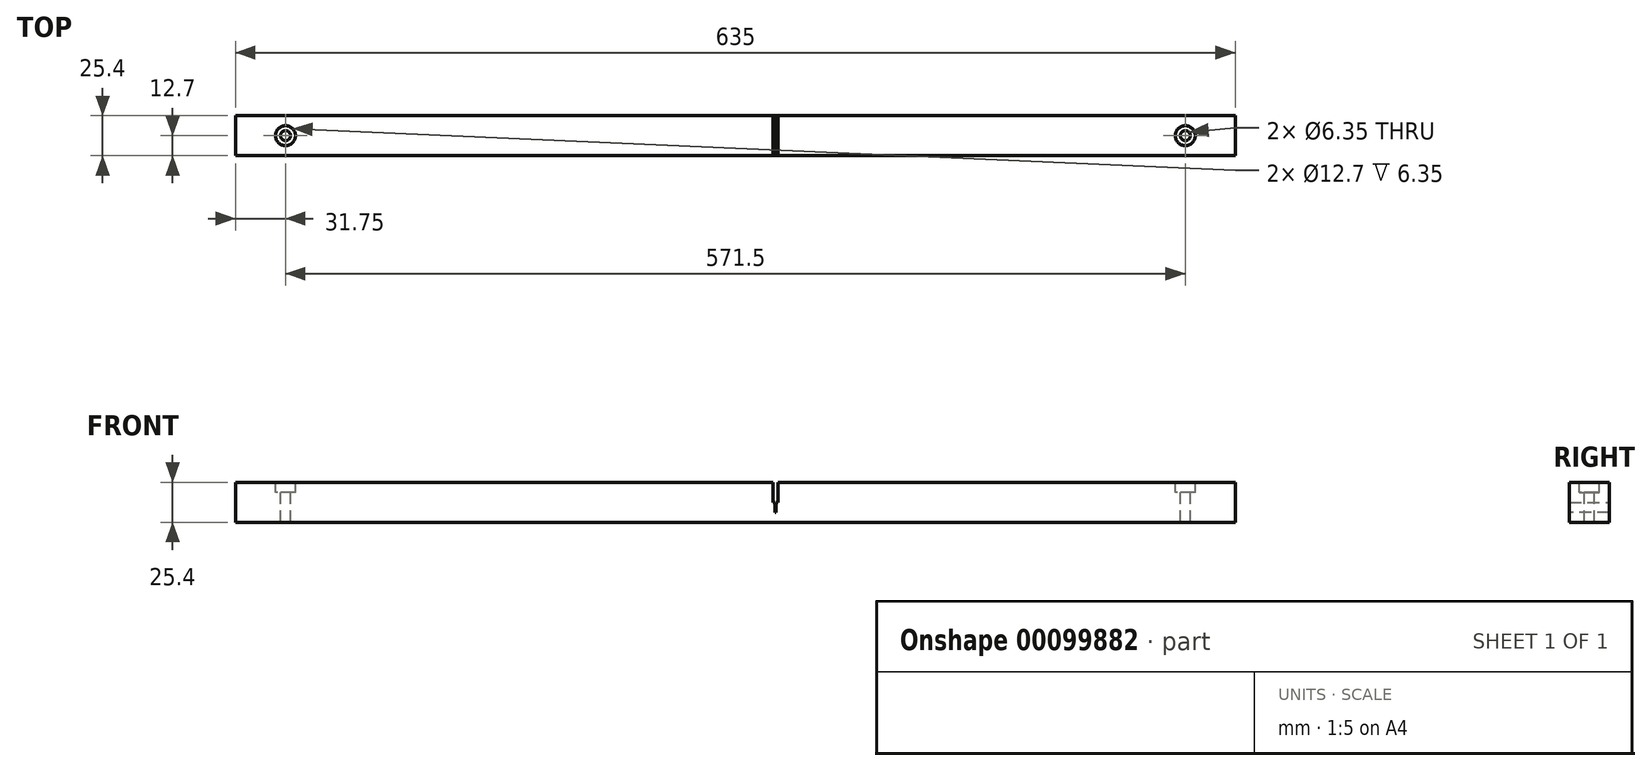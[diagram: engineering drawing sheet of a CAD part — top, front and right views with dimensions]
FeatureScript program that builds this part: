
annotation { "Feature Type Name" : "Feature", "Feature Type Description" : "" }
export const myFeature = defineFeature(function(context is Context, id is Id, definition is map)
    precondition{}
    {
        {
            var Q0;
            Q0=qCreatedBy(makeId("Top.planeOp"),FACE);
            var sketch = newSketch(context, id + "F0", { "sketchPlane" : qUnion([Q0])});
            skLineSegment(sketch, "E0.bottom", {"start": v(317.5, -12.7) * mm, "end": v(-317.5, -12.7) * mm});
            skLineSegment(sketch, "E0.top", {"start": v(317.5, 12.7) * mm, "end": v(-317.5, 12.7) * mm});
            skLineSegment(sketch, "E0.left", {"start": v(317.5, -12.7) * mm, "end": v(317.5, 12.7) * mm});
            skLineSegment(sketch, "E0.right", {"start": v(-317.5, -12.7) * mm, "end": v(-317.5, 12.7) * mm});
            skPoint(sketch, "E0.middle", {"position": v(0, 0) * mm});
            skSolve(sketch);
        }
        {
            var Q0;
            Q0=makeQuery(id+"F0.imprint","IMPRINT",FACE,{"disambiguationData":[TD([[makeQuery(id+"F0.imprint","IMPRINT",EDGE,{"derivedFrom":sQuery(id+"F0.wireOp",EDGE,"E0.bottom")}),-1.0]])]});
            extrude(context, id + "F1", {"entities" : qUnion([Q0]), "depth" : 25.4 * mm});
        }
        {
            var Q0;
            Q0=makeQuery(id+"F1.opExtrude","CAP_FACE",FACE,{"disambiguationData":[OSD([sQuery(id+"F0.wireOp",EDGE,"E0.bottom"),sQuery(id+"F0.wireOp",EDGE,"E0.top"),sQuery(id+"F0.wireOp",EDGE,"E0.left"),sQuery(id+"F0.wireOp",EDGE,"E0.right")])],"isStart":false});
            var sketch = newSketch(context, id + "F2", { "sketchPlane" : qUnion([Q0])});
            skPoint(sketch, "E1", {"position": v(-285.75, 0) * mm});
            skPoint(sketch, "E2.MirrorP", {"position": v(285.75, 0) * mm});
            skSolve(sketch);
        }
        {
            var Q0;
            Q0=sQuery(id+"F2.wireOp",VERTEX,"E1");
            var Q1;
            Q1=sQuery(id+"F2.wireOp",VERTEX,"E2.MirrorP");
            var Q2;
            Q2=makeQuery(id+"F1.opExtrude","SWEPT_BODY",BODY,{"disambiguationData":[OSD([sQuery(id+"F0.wireOp",EDGE,"E0.bottom"),sQuery(id+"F0.wireOp",EDGE,"E0.top"),sQuery(id+"F0.wireOp",EDGE,"E0.left"),sQuery(id+"F0.wireOp",EDGE,"E0.right")])]});
            hole(context, id + "F3", {"style" : HoleStyle.C_BORE, "endStyle" : HoleEndStyle.THROUGH, "holeDiameter" : 6.35 * mm, "cBoreDiameter" : 12.7 * mm, "cBoreDepth" : 6.35 * mm, "locations" : qUnion([Q0, Q1]), "scope" : qUnion([Q2]), "isTappedThrough" : true});
        }
        {
            var Q0;
            Q0=makeQuery(id+"F1.opExtrude","CAP_FACE",FACE,{"disambiguationData":[OSD([sQuery(id+"F0.wireOp",EDGE,"E0.bottom"),sQuery(id+"F0.wireOp",EDGE,"E0.top"),sQuery(id+"F0.wireOp",EDGE,"E0.left"),sQuery(id+"F0.wireOp",EDGE,"E0.right")])],"isStart":false});
            var sketch = newSketch(context, id + "F4", { "sketchPlane" : qUnion([Q0])});
            skLineSegment(sketch, "E3.bottom", {"start": v(25.1, 12.7) * mm, "end": v(25.7, 12.7) * mm});
            skLineSegment(sketch, "E3.top", {"start": v(25.1, -12.7) * mm, "end": v(25.7, -12.7) * mm});
            skLineSegment(sketch, "E3.left", {"start": v(25.1, 12.7) * mm, "end": v(25.1, -12.7) * mm});
            skLineSegment(sketch, "E3.right", {"start": v(25.7, 12.7) * mm, "end": v(25.7, -12.7) * mm});
            skPoint(sketch, "E3.middle", {"position": v(25.4, 0) * mm});
            skSolve(sketch);
        }
        {
            var Q0;
            Q0 = qSketchRegion(id + "F4", true);
            extrude(context, id + "F5", {"entities" : qUnion([Q0]), "operationType" : NewBodyOperationType.REMOVE, "oppositeDirection" : true, "depth" : 19.05 * mm});
        }
        {
            var Q0;
            {var subQ0=sQuery(id+"F0.wireOp",EDGE,"E0.right");var subQ1=sQuery(id+"F0.wireOp",EDGE,"E0.top");var subQ2=sQuery(id+"F0.wireOp",EDGE,"E0.bottom");Q0=makeQuery(id+"F5.boolean.opBoolean","SPLIT",FACE,{"disambiguationData":[TD([makeQuery(id+"F1.opExtrude","SWEPT_FACE",FACE,{"disambiguationData":[OSD([subQ0])]})])],"derivedFrom":makeQuery(id+"F1.opExtrude","CAP_FACE",FACE,{"disambiguationData":[OSD([subQ2,subQ1,sQuery(id+"F0.wireOp",EDGE,"E0.left"),subQ0])],"isStart":false})});}
            var sketch = newSketch(context, id + "F6", { "sketchPlane" : qUnion([Q0])});
            skLineSegment(sketch, "E4", {"start": v(25.1, 12.7) * mm, "end": v(25.7, 12.7) * mm, "construction": true});
            skLineSegment(sketch, "E5", {"start": v(25.4, 12.7) * mm, "end": v(25.4, 0) * mm, "construction": true});
            skLineSegment(sketch, "E6.bottom", {"start": v(23.81, -12.7) * mm, "end": v(26.99, -12.7) * mm});
            skLineSegment(sketch, "E6.top", {"start": v(23.81, 12.7) * mm, "end": v(26.99, 12.7) * mm});
            skLineSegment(sketch, "E6.left", {"start": v(23.81, -12.7) * mm, "end": v(23.81, 12.7) * mm});
            skLineSegment(sketch, "E6.right", {"start": v(26.99, -12.7) * mm, "end": v(26.99, 12.7) * mm});
            skPoint(sketch, "E6.middle", {"position": v(25.4, 0) * mm});
            skSolve(sketch);
        }
        {
            var Q0;
            Q0 = qSketchRegion(id + "F6", true);
            extrude(context, id + "F7", {"entities" : qUnion([Q0]), "operationType" : NewBodyOperationType.REMOVE, "oppositeDirection" : true, "depth" : 12.7 * mm});
        }
    });
